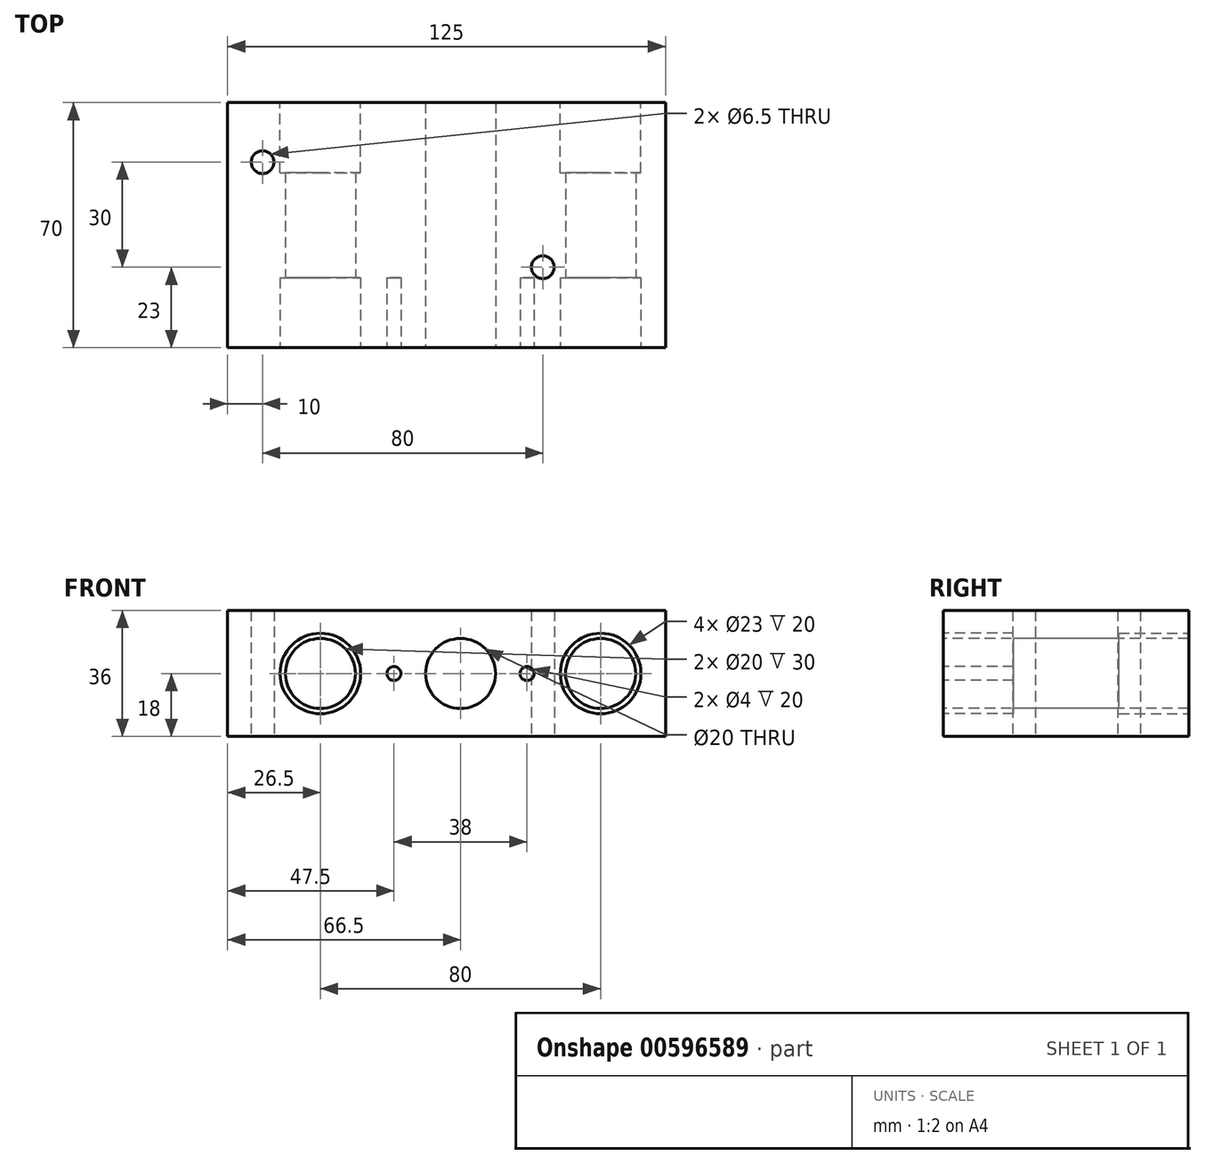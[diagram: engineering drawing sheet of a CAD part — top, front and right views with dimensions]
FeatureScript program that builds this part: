
annotation { "Feature Type Name" : "Feature", "Feature Type Description" : "" }
export const myFeature = defineFeature(function(context is Context, id is Id, definition is map)
    precondition{}
    {
        {
            var Q0;
            Q0=qCreatedBy(makeId("Top.planeOp"),FACE);
            var sketch = newSketch(context, id + "F0", { "sketchPlane" : qUnion([Q0])});
            skLineSegment(sketch, "E0.bottom", {"start": v(0, 0) * mm, "end": v(125, 0) * mm});
            skLineSegment(sketch, "E0.top", {"start": v(0, 70) * mm, "end": v(125, 70) * mm});
            skLineSegment(sketch, "E0.left", {"start": v(0, 0) * mm, "end": v(0, 70) * mm});
            skLineSegment(sketch, "E0.right", {"start": v(125, 0) * mm, "end": v(125, 70) * mm});
            skSolve(sketch);
        }
        {
            var Q0;
            Q0=makeQuery(id+"F0.imprint","IMPRINT",FACE,{"disambiguationData":[TD([[makeQuery(id+"F0.imprint","IMPRINT",EDGE,{"derivedFrom":sQuery(id+"F0.wireOp",EDGE,"E0.bottom")}),1.0]])]});
            extrude(context, id + "F1", {"entities" : qUnion([Q0]), "depth" : 36 * mm, "offsetDistance" : 25 * mm});
        }
        {
            var Q0;
            Q0=makeQuery(id+"F1.opExtrude","SWEPT_FACE",FACE,{"disambiguationData":[OSD([sQuery(id+"F0.wireOp",EDGE,"E0.bottom")])]});
            var sketch = newSketch(context, id + "F2", { "sketchPlane" : qUnion([Q0])});
            skCircle(sketch, "E1", {"center": v(26.5, 18) * mm, "radius": 10 * mm});
            skCircle(sketch, "E2", {"center": v(66.5, 18) * mm, "radius": 10 * mm});
            skCircle(sketch, "E3", {"center": v(106.5, 18) * mm, "radius": 10 * mm});
            skSolve(sketch);
        }
        {
            var Q0;
            Q0 = qSketchRegion(id + "F2", true);
            extrude(context, id + "F3", {"entities" : qUnion([Q0]), "operationType" : NewBodyOperationType.REMOVE, "endBound" : BoundingType.THROUGH_ALL, "oppositeDirection" : true, "depth" : 25 * mm, "offsetDistance" : 25 * mm});
        }
        {
            var Q0;
            Q0=makeQuery(id+"F1.opExtrude","SWEPT_FACE",FACE,{"disambiguationData":[OSD([sQuery(id+"F0.wireOp",EDGE,"E0.bottom")])]});
            var sketch = newSketch(context, id + "F4", { "sketchPlane" : qUnion([Q0])});
            skCircle(sketch, "E4", {"center": v(26.5, 18) * mm, "radius": 11.5 * mm});
            skCircle(sketch, "E5", {"center": v(106.5, 18) * mm, "radius": 11.5 * mm});
            skSolve(sketch);
        }
        {
            var Q0;
            Q0=makeQuery(id+"F4.imprint","IMPRINT",FACE,{"disambiguationData":[TD([[makeQuery(id+"F4.imprint","IMPRINT",EDGE,{"derivedFrom":sQuery(id+"F4.wireOp",EDGE,"E4")}),1.0]])]});
            var Q1;
            Q1=makeQuery(id+"F4.imprint","IMPRINT",FACE,{"disambiguationData":[TD([[makeQuery(id+"F4.imprint","IMPRINT",EDGE,{"derivedFrom":sQuery(id+"F4.wireOp",EDGE,"E5")}),1.0]])]});
            extrude(context, id + "F5", {"entities" : qUnion([Q0, Q1]), "operationType" : NewBodyOperationType.REMOVE, "oppositeDirection" : true, "depth" : 20 * mm, "offsetDistance" : 25 * mm});
        }
        {
            var Q0;
            Q0=makeQuery(id+"F1.opExtrude","SWEPT_FACE",FACE,{"disambiguationData":[OSD([sQuery(id+"F0.wireOp",EDGE,"E0.top")])]});
            var sketch = newSketch(context, id + "F6", { "sketchPlane" : qUnion([Q0])});
            skCircle(sketch, "E6", {"center": v(-106.5, 18) * mm, "radius": 11.5 * mm});
            skCircle(sketch, "E7", {"center": v(-26.5, 18) * mm, "radius": 11.5 * mm});
            skSolve(sketch);
        }
        {
            var Q0;
            Q0=makeQuery(id+"F6.imprint","IMPRINT",FACE,{"disambiguationData":[TD([[makeQuery(id+"F6.imprint","IMPRINT",EDGE,{"derivedFrom":sQuery(id+"F6.wireOp",EDGE,"E6")}),1.0]])]});
            var Q1;
            Q1=makeQuery(id+"F6.imprint","IMPRINT",FACE,{"disambiguationData":[TD([[makeQuery(id+"F6.imprint","IMPRINT",EDGE,{"derivedFrom":sQuery(id+"F6.wireOp",EDGE,"E7")}),1.0]])]});
            extrude(context, id + "F7", {"entities" : qUnion([Q0, Q1]), "operationType" : NewBodyOperationType.REMOVE, "oppositeDirection" : true, "depth" : 20 * mm, "offsetDistance" : 25 * mm});
        }
        {
            var Q0;
            Q0=makeQuery(id+"F1.opExtrude","CAP_FACE",FACE,{"disambiguationData":[OSD([sQuery(id+"F0.wireOp",EDGE,"E0.bottom"),sQuery(id+"F0.wireOp",EDGE,"E0.top"),sQuery(id+"F0.wireOp",EDGE,"E0.left"),sQuery(id+"F0.wireOp",EDGE,"E0.right")])],"isStart":true});
            var sketch = newSketch(context, id + "F8", { "sketchPlane" : qUnion([Q0])});
            skCircle(sketch, "E8", {"center": v(90, -23) * mm, "radius": 3.25 * mm});
            skCircle(sketch, "E9", {"center": v(125.05, 12.9) * mm, "radius": 12.9 * mm});
            skCircle(sketch, "E10", {"center": v(10, -53) * mm, "radius": 3.25 * mm});
            skSolve(sketch);
        }
        {
            var Q0;
            Q0 = qSketchRegion(id + "F8", true);
            extrude(context, id + "F9", {"entities" : qUnion([Q0]), "operationType" : NewBodyOperationType.REMOVE, "endBound" : BoundingType.THROUGH_ALL, "oppositeDirection" : true, "depth" : 25 * mm, "offsetDistance" : 25 * mm});
        }
        {
            var Q0;
            Q0=makeQuery(id+"F1.opExtrude","SWEPT_FACE",FACE,{"disambiguationData":[OSD([sQuery(id+"F0.wireOp",EDGE,"E0.bottom")])]});
            var sketch = newSketch(context, id + "F10", { "sketchPlane" : qUnion([Q0])});
            skCircle(sketch, "E11", {"center": v(66.5, 18) * mm, "radius": 19 * mm, "construction": true});
            skCircle(sketch, "E12", {"center": v(47.5, 18) * mm, "radius": 2 * mm});
            skCircle(sketch, "E13", {"center": v(85.5, 18) * mm, "radius": 2 * mm});
            skSolve(sketch);
        }
        {
            var Q0;
            Q0 = qSketchRegion(id + "F10", true);
            extrude(context, id + "F11", {"entities" : qUnion([Q0]), "operationType" : NewBodyOperationType.REMOVE, "oppositeDirection" : true, "depth" : 20 * mm, "offsetDistance" : 25 * mm});
        }
    });
